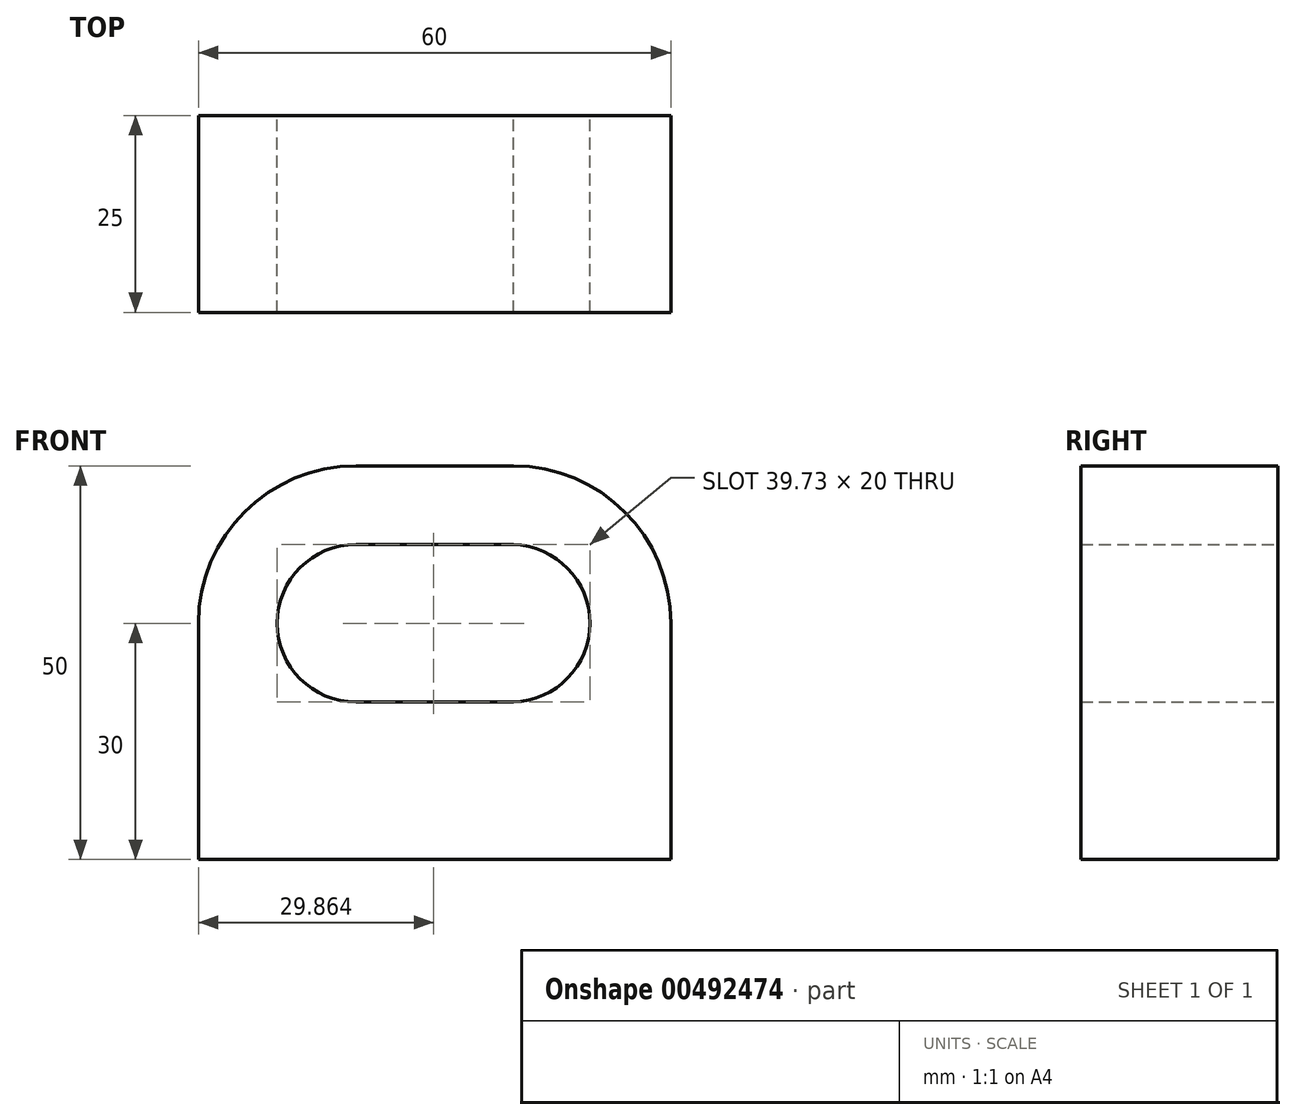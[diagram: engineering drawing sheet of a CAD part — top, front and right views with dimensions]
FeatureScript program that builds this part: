
annotation { "Feature Type Name" : "Feature", "Feature Type Description" : "" }
export const myFeature = defineFeature(function(context is Context, id is Id, definition is map)
    precondition{}
    {
        {
            var Q0;
            Q0=qCreatedBy(makeId("Front.planeOp"),FACE);
            var sketch = newSketch(context, id + "F0", { "sketchPlane" : qUnion([Q0])});
            skLineSegment(sketch, "E0.bottom", {"start": v(-10, 25) * mm, "end": v(10, 25) * mm});
            skLineSegment(sketch, "E0.top", {"start": v(-30, -25) * mm, "end": v(30, -25) * mm});
            skLineSegment(sketch, "E0.left", {"start": v(-30, 5) * mm, "end": v(-30, -25) * mm});
            skLineSegment(sketch, "E0.right", {"start": v(30, 5) * mm, "end": v(30, -25) * mm});
            skPoint(sketch, "E0.middle", {"position": v(0, 0) * mm});
            skPoint(sketch, "E1.visualSharp", {"position": v(-30, 25) * mm});
            skArc(sketch, "E1.filletArc", {"start": v(-10, 25) * mm, "mid": v(-24.14, 19.14) * mm, "end": v(-30, 5) * mm});
            skPoint(sketch, "E2.visualSharp", {"position": v(30, 25) * mm});
            skArc(sketch, "E2.filletArc", {"start": v(30, 5) * mm, "mid": v(24.14, 19.14) * mm, "end": v(10, 25) * mm});
            skArc(sketch, "E3", {"start": v(-10, 15) * mm, "mid": v(-20, 5) * mm, "end": v(-10, -5) * mm});
            skArc(sketch, "E4", {"start": v(10, -5) * mm, "mid": v(19.73, 5) * mm, "end": v(10, 15) * mm});
            skLineSegment(sketch, "E5", {"start": v(-10, 15) * mm, "end": v(10, 15) * mm});
            skLineSegment(sketch, "E6", {"start": v(-10, -5) * mm, "end": v(10, -5) * mm});
            skSolve(sketch);
        }
        {
            var Q0;
            Q0=makeQuery(id+"F0.imprint","IMPRINT",FACE,{"disambiguationData":[TD([[makeQuery(id+"F0.imprint","IMPRINT",EDGE,{"derivedFrom":sQuery(id+"F0.wireOp",EDGE,"E0.bottom")}),-1.0]])]});
            extrude(context, id + "F1", {"entities" : qUnion([Q0]), "depth" : 25 * mm});
        }
    });
